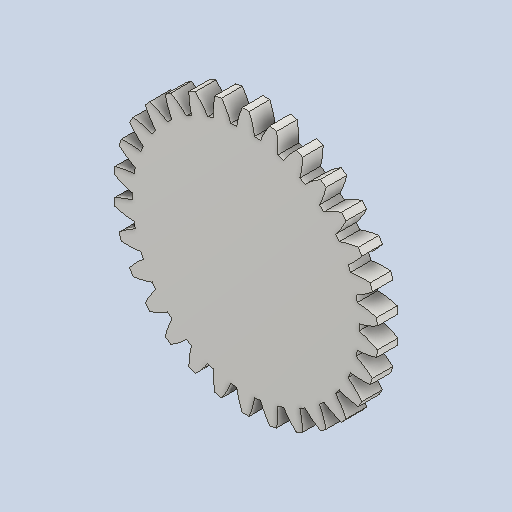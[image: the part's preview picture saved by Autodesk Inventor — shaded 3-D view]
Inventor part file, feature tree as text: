
AUTODESK INVENTOR PART (.ipt)
format: ipt  version: 2024 (Build 280153000, 153)  size: 259,072 bytes
history: native  units: mm (DEFAULTED — no unit token found)
features: plane x3, other x3, extrude x1, sketch x1
ambient origin geometry x8: Origin, YZ Plane, XZ Plane, XY Plane, X Axis, Y Axis, Z Axis, Center Point
bodies: Solid1 (feature_tree)
feature tree (8):
  extrude  "Extrusion1"  Depth=5.0mm TaperAngle=0.0deg
  plane  "Work Plane2"
  plane  "Work Plane8"
  plane  "Work Plane9"
  other  "Spur Gear"
  sketch  "Sketch1"  dims[d0=64.0mm d1=5.0mm d2=0.0mm d3=60.0mm d4=10.0mm d5=0.0mm d16=120.0mm d17=0.0mm d34=1.047198mm d39=0.0mm d41=0.0mm d43=120.0mm d46=120.0mm d47=0.0mm d48=0.0mm]
  other  "Srf1"
  other  "Pitch Diameter"
